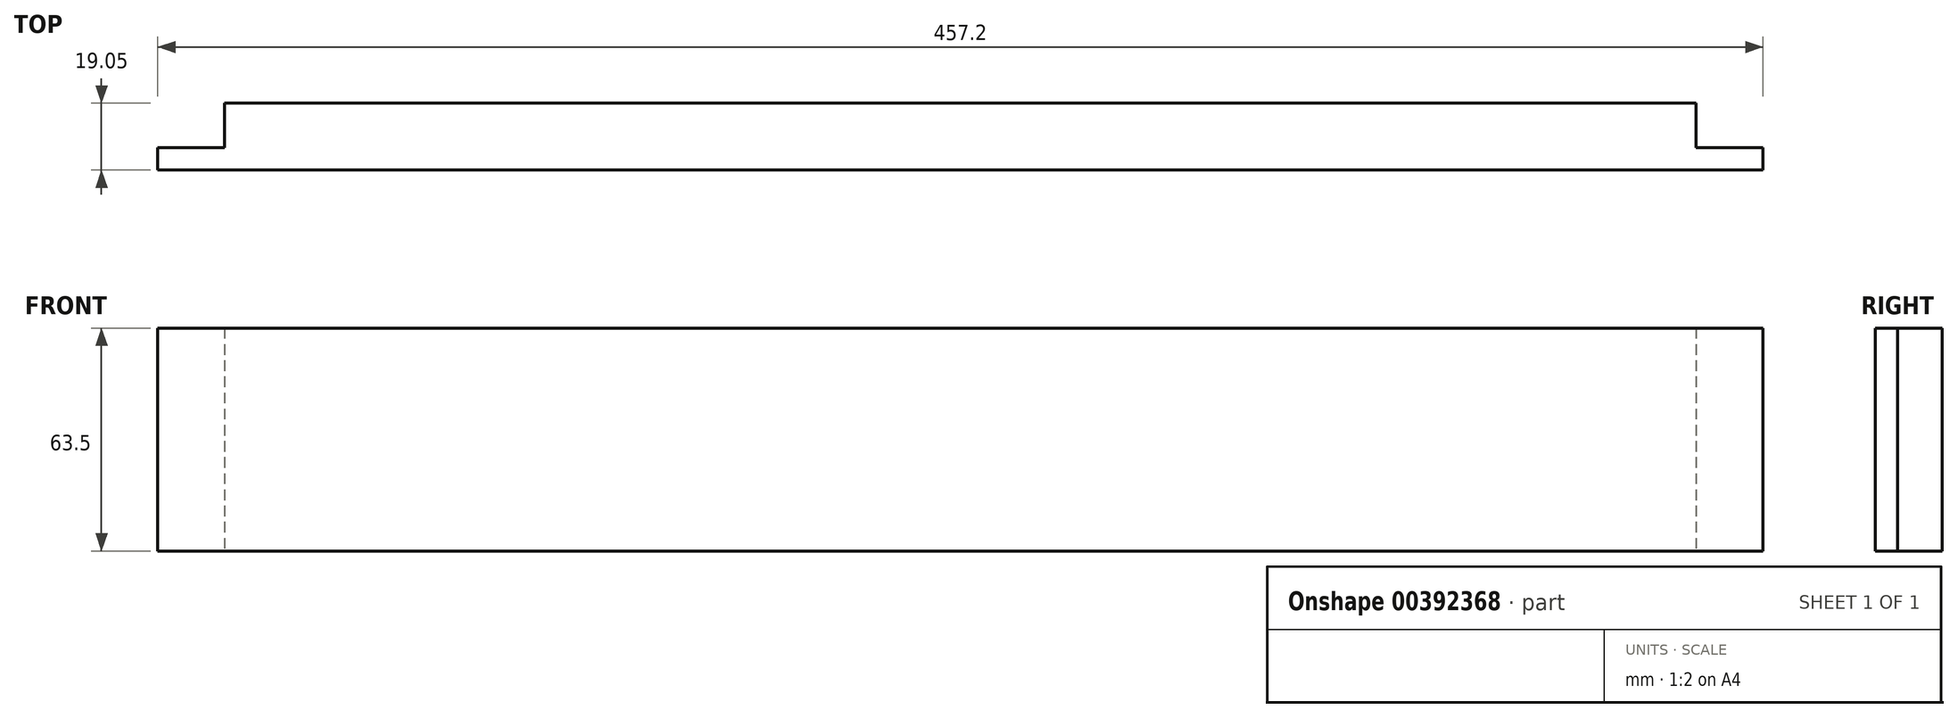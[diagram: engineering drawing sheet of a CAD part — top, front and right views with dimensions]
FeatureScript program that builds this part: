
annotation { "Feature Type Name" : "Feature", "Feature Type Description" : "" }
export const myFeature = defineFeature(function(context is Context, id is Id, definition is map)
    precondition{}
    {
        {
            var Q0;
            Q0=qCreatedBy(makeId("Top.planeOp"),FACE);
            var sketch = newSketch(context, id + "F0", { "sketchPlane" : qUnion([Q0])});
            skLineSegment(sketch, "E0.bottom", {"start": v(-209.55, 0) * mm, "end": v(209.55, 0) * mm});
            skLineSegment(sketch, "E0.top", {"start": v(-228.6, -19.05) * mm, "end": v(228.6, -19.05) * mm});
            skLineSegment(sketch, "E0.left", {"start": v(-228.6, -12.7) * mm, "end": v(-228.6, -19.05) * mm});
            skLineSegment(sketch, "E0.right", {"start": v(228.6, -12.7) * mm, "end": v(228.6, -19.05) * mm});
            skLineSegment(sketch, "E1", {"start": v(-209.55, 0) * mm, "end": v(-209.55, -12.7) * mm});
            skLineSegment(sketch, "E2", {"start": v(-209.55, -12.7) * mm, "end": v(-228.6, -12.7) * mm});
            skPoint(sketch, "E2.endSnap0", {"position": v(-228.6, -9.52) * mm});
            skLineSegment(sketch, "E3", {"start": v(228.6, -12.7) * mm, "end": v(209.55, -12.7) * mm});
            skLineSegment(sketch, "E4", {"start": v(209.55, -12.7) * mm, "end": v(209.55, 0) * mm});
            skPoint(sketch, "E5.orphan", {"position": v(-228.6, 0) * mm});
            skSolve(sketch);
        }
        {
            var Q0;
            Q0=makeQuery(id+"F0.imprint","IMPRINT",FACE,{"disambiguationData":[TD([[makeQuery(id+"F0.imprint","IMPRINT",EDGE,{"derivedFrom":sQuery(id+"F0.wireOp",EDGE,"E0.bottom")}),-1.0]])]});
            extrude(context, id + "F1", {"entities" : qUnion([Q0]), "depth" : 63.5 * mm});
        }
    });
